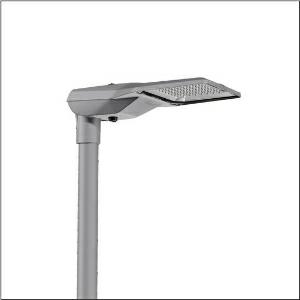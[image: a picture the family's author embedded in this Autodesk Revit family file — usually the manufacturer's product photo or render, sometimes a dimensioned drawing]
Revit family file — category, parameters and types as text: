
# Revit family: streetlight_sl_21_midi___p0_8ab_5xe3r33t08lb_8313
name_source: partatom
category: Lighting Fixtures
units: mm (PartAtom-declared; Revit-internal decimal feet)

## family parameters
Cut with Voids When Loaded = No
Host = Face
Light Source = No
Part Type = Normal
Room Calculation Point = No
Round Connector Dimension = Use Diameter
Shared = No

## types (1)
- --- (1 x LED, 12450 lm, 99.6 W, 3000K)
    Apparent Load = 100 VA
    CIE Flux Codes = 36 71 98 100 100
    Color Rendering = 70
    Color Temperature = 3000K
    Default Elevation = 1800 mm
    Description = Streetlight SL 21 midi, mast luminaire, primary light control with lens, of PMMA, primary optical cover: cover, of toughened safety glass, transparent, light distribution: P0.8aB, light emission: direct distribution, primary light characteristic: asymmetric, installation type: post-top, side-entry, LED, High Power LED, rated luminous flux: 12.450lm, luminous efficacy: 125lm/W, light colour: 730, colour temperature: 3000K, control gear: D4i, control: pre-setting: logarithmic dimming characteristic, flexible luminous flux parameterisation, time-dependent luminous flux control, constant luminous flux control, overheat protection, mains connection: 230..240V, AC, 50/60Hz, start of lifetime: 100W, end of service life: 102W, reduction: 46W, luminaire housing, of diecast aluminium, powder-coated, SITECO metallic grey (DB 702S), corrosivity category C5 high according to DIN EN ISO 12944, multi-level sealing system, sealing non-destructively replaceable, inclination adjustable: 0°, 5°, 10°, 15°, please order mast flange separately, length: 644mm, width: 335mm, height: 110mm, mast flange for spigot size: 42mm (side-entry): 5XC10008XM4, 60/48mm (side-entry/post-top): 5XC10108XM2, 76/60mm (side-entry/post-top): 5XC10108XM1, mounting height: 4..8m, Smart Interface below and above, protection rating (complete): IP66, insulation class (complete): insulation class II (safety insulation), certification: CE, ENEC, ENEC+, VDE, impact resistance: IK10, permissible operating ambient temperature for outdoor applications: -40..+50°C, standard-compliant lighting for roads and squares, packaging unit: 1 piece

Light Distribution: P0.8aB
    Height = 111 mm
    Lamp = 1 x LED
    Lamp Light Flux = 12450 lm
    Lamp Power = 99.6 W
    Lamp count = 1
    Length = 644 mm
    Luminous efficacy = 125 lm/W
    Manufacturer = Siteco
    ModVariant = No
    Model = 5XE3R33T08LB
    Number of Poles = 1
    OnlyDefault = Yes
    Power Factor = 1
    Product Name = Streetlight SL 21 midi | P0.8aB
    Product group = mast luminaire | pylon top
    ProductGroupID = 6100
    Protection Class = Protection class II
    Protection Degree = IP 66
    RLX_Detail_Level = 1
    RLX_Emergency_Light_Flux = 0 lm
    RLX_Emergency_Type = 0
    RLX_Emergency_Type_DB = No
    RlxData = <blob elided: 26597 chars, md5=81db89c0>
    Socket = socket
    Standby Power = 0 W
    System Light Flux = 12450 lm
    System Power = 100 W
    Type Comments = factory setting: luminous flux: 100 % | dim-lin: 254 | 1020 mA
    Type Image = l_1004304.jpg
    URL = http://relux.com
    VarID = @adj_033267
    Voltage = 0 V
    Weight = 0.00 kg
    Width = 336 mm

## geometry (parser evidence)
native form markers: Blend x4, Sweep x11
no freeform markers — native parametric forms only
